# Revit family: Faucet-Lavatory-KOHLER-Triton-K-7443
name_source: partatom
category: Plumbing Fixtures
revit_build: Autodesk Revit 2017 (Build: 20160225_1515(x64)
units: mm (PartAtom-declared; Revit-internal decimal feet)

## family parameters
Cut with Voids When Loaded = No
Host = Face
OmniClass Number = 23.31.11.00
OmniClass Title = Faucets
Part Type = Normal
Room Calculation Point = No
Round Connector Dimension = Use Diameter
Shared = No

## types (6) — shared parameters
ADA Compliant = No
Assembly Code = D2010
CW Connection = Yes
Cold Water Inlet = Cold Water Inlet
Date Modified = 10/20/2020
Default Elevation = 36"
Drain Included = No
Finish = Kohler-Metal-CP-Polished_Chrome
HW Connection = Yes
Height = 2 3/4"
Hot Water Inlet = Hot Water Inlet
Length = 5"
Manufacturer = KOHLER Co.
Master Format 2014 = 22 41 39
Master Format 2014 Name = Residential Faucets, Supplies, and Trim
Material = Brass Construction
Pressure = 60.00 psi
Product Documentation Link = https://www.us.kohler.com
Product Name = Triton
Product Page URL = https://www.us.kohler.com
Spout Reach = 5"
URL = https://www.us.kohler.com
Vent Connection = No
Waste Connection = No
Waste Water Outlet = Waste Water Outlet
WaterSense Certified = No

## per-type parameters (varying)
| type | Description | Dick Valve | Flow Rate | Handle Clearance | Model | Standard Handle | Type |
| 0.5 GPM, Standard Handle,CP- Polished Chrome | 0.5 gpm widespread commercial bathroom sink faucet with standard handles, drain not included | No | 1 GPM | 2 3/4" | K-7443-2N-CP | Yes | 1 |
| 0.5 GPM, Disk Valve,CP- Polished Chrome | 0.5 gpm widespread commercial bathroom sink base faucet, requires handles, drain not included | Yes | 1 GPM | 0" | K-7443-KN-CP | No | 2 |
| 0.5 GPM, Vandal-Resistant Aerator, CP- Polished Chrome | 0.5 gpm widespread commercial bathroom sink base faucet with vandal-resistant aerator, requires handles, drain not included | Yes | 1 GPM | 0" | K-7443-KNE-CP | No | 3 |
| 2 GPM, Standard Handle, CP- Polished Chrome | Widespread commercial bathroom sink faucet with standard handles, drain not included | No | 2 GPM | 2 3/4" | K-7443-2A-CP | Yes | 4 |
| 2 GPM, Disk Valve,CP- Polished Chrome | Widespread commercial bathroom sink faucet, drain not included and lift rod, requires handles | Yes | 2 GPM | 0" | K-7443-K-CP | No | 5 |
| 2 GPM,Vandal Resistant Aerator,Disk Valve,CP- Polished Chrome | Widespread commercial bathroom sink faucet with vandal-resistant aerator, requires handles, drain not included | Yes | 2 GPM | 0" | K-7443-KE-CP | No | 6 |

## geometry (parser evidence)
native form markers: Sweep x8
no freeform markers — native parametric forms only
